# Revit family: BDG_BossDesign_Qube Solo
name_source: partatom
category: Furniture
revit_build: Autodesk Revit 2018 (Build: 20190510_1515(x64)
units: mm (PartAtom-declared; Revit-internal decimal feet)

## family parameters
Always vertical = Yes
Cut with Voids When Loaded = No
Room Calculation Point = No
Shared = Yes
Work Plane-Based = No

## types (1)
- Qube Solo
    BIMObjectName = BDG_BossDesign_QubeSolo
    Description = Qube Solo
    Features = Powder coated frame available
    Finish = Manifestations on Glass
    ManufacturerName = Boss Design
    ManufacturerURL = www.bossdesign.com
    Material = Glass
    Model = QSolo
    ModelNumber = QSolo
    ModelReference = Qube Solo
    Name = PanelPartitions_QubeSolo_BossDesign
    Nominal Depth = 1440 mm  [stored 4.72441 ft]
    Nominal Height = 2225 mm
    Nominal Width = 1100 mm
    ProductInformation = https://www.bossdesign.com
    Shape = Rectangular
    Size = 1100 x 1440 x 2225mm
    URL = www.bossdesign.com
    Version = 1

note: [stored X ft] marks values corroborated as IEEE doubles in the binary element streams (Revit-internal decimal feet)

## geometry (parser evidence)
native form markers: Sweep x2
no freeform markers — native parametric forms only
